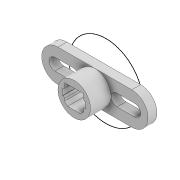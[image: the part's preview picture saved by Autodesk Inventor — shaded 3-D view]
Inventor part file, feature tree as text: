
AUTODESK INVENTOR PART (.ipt)
format: ipt  version: 2022 (Build 260153000, 153)  size: 226,816 bytes
history: native  units: in
note: dims shown in document units (in); Inventor stores cm internally (conversion verified against a paired STEP export)
features: sketch x3, other x2, extrude x2, projected_geometry x1
ambient origin geometry x8: Origin, YZ Plane, XZ Plane, XY Plane, X Axis, Y Axis, Z Axis, Center Point
bodies: Volumenkörper1 (feature_tree)
feature tree (8):
  other  "00_toslink_launcher_v3"
  sketch  "Skizze1"  dims[d0=0.4331in d1=0.3937in d2=0.0in]
  extrude  "Extrusion1"  Depth=0.3937in TaperAngle=0.0deg
  extrude  "Extrusion2"  Depth=0.1181in
  sketch  "Skizze2"  dims[d3=0.4921in d4=0.1181in]
  sketch  "Skizze3"  dims[d5=0.1575in d6=0.1181in d7=0.1575in d8=0.4134in d9=0.4134in d10=0.1181in d11=0.0in]
  projected_geometry  "Projizierte Kontur1"
  other  "MeshFeature1"
